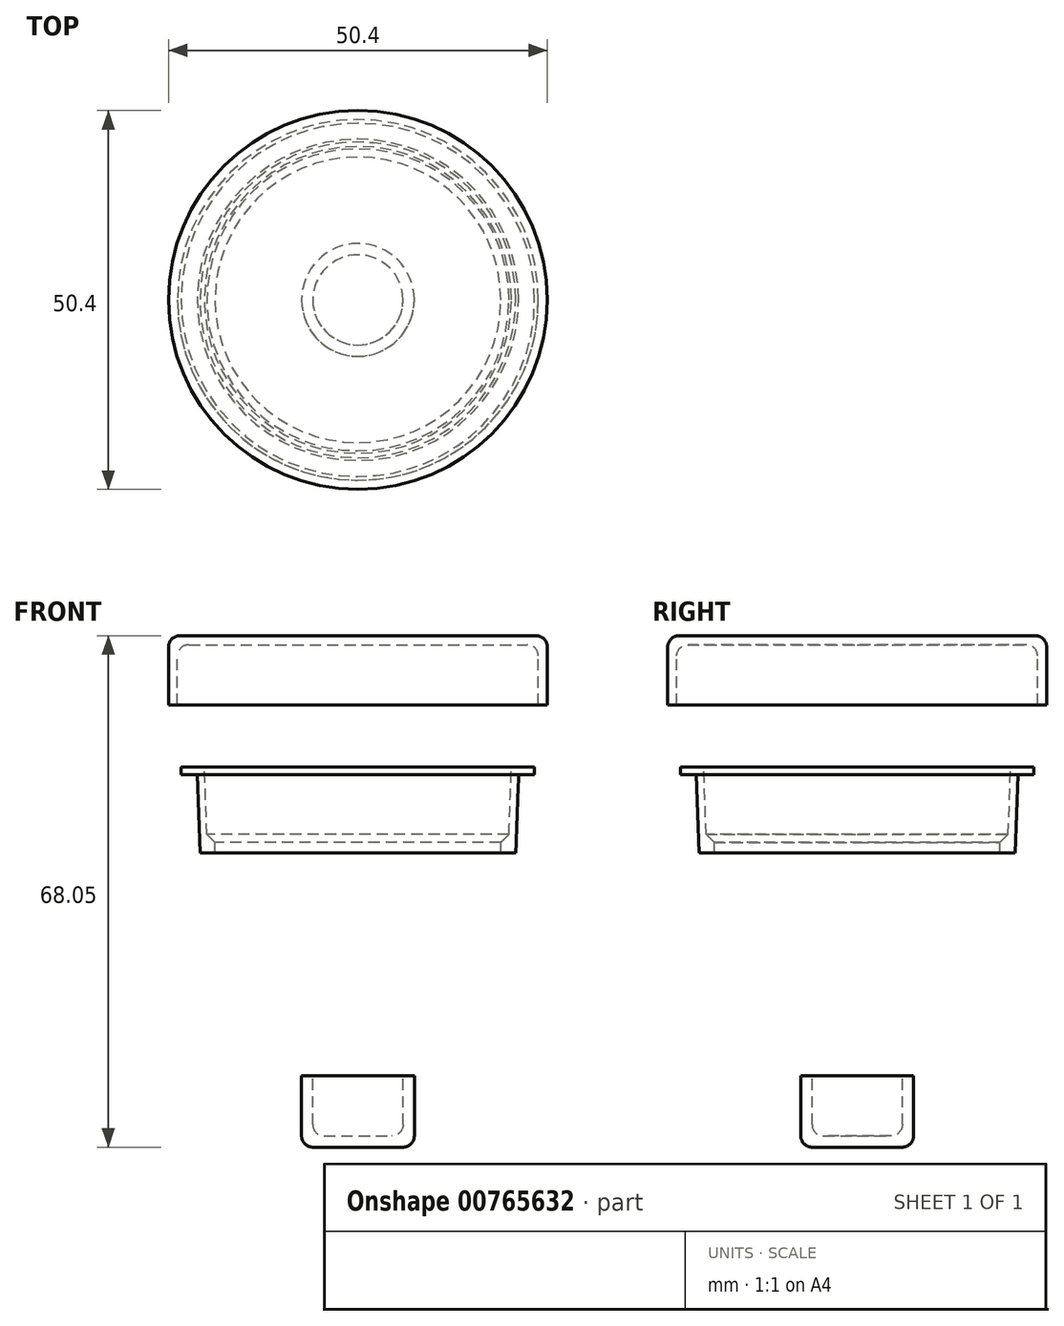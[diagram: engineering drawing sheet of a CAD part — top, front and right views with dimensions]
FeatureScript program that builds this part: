
annotation { "Feature Type Name" : "Feature", "Feature Type Description" : "" }
export const myFeature = defineFeature(function(context is Context, id is Id, definition is map)
    precondition{}
    {
        {
            var Q0;
            Q0=qCreatedBy(makeId("Front.planeOp"),FACE);
            var sketch = newSketch(context, id + "F0", { "sketchPlane" : qUnion([Q0])});
            skLineSegment(sketch, "E0", {"start": v(0, 66.35) * mm, "end": v(0, -60.94) * mm, "construction": true});
            skLineSegment(sketch, "E1", {"start": v(-23.5, 22.12) * mm, "end": v(-21.37, 22.12) * mm});
            skLineSegment(sketch, "E2", {"start": v(-21.38, 22.12) * mm, "end": v(-21, 11.72) * mm});
            skLineSegment(sketch, "E3", {"start": v(-21, 11.72) * mm, "end": v(-19, 11.72) * mm});
            skLineSegment(sketch, "E4.0", {"start": v(-23.5, 23.12) * mm, "end": v(-21.37, 23.12) * mm});
            skLineSegment(sketch, "E5.0", {"start": v(-20.38, 22.15) * mm, "end": v(-20.04, 12.72) * mm});
            skLineSegment(sketch, "E6", {"start": v(-20.04, 12.72) * mm, "end": v(-19, 12.72) * mm});
            skLineSegment(sketch, "E7", {"start": v(-20.38, 22.15) * mm, "end": v(-20.41, 23.12) * mm});
            skLineSegment(sketch, "E8", {"start": v(-21.37, 23.12) * mm, "end": v(-20.41, 23.12) * mm});
            skLineSegment(sketch, "E9", {"start": v(-23.5, 23.12) * mm, "end": v(-23.5, 22.12) * mm});
            skLineSegment(sketch, "E10", {"start": v(-19, 12.72) * mm, "end": v(-19, 11.72) * mm});
            skSolve(sketch);
        }
        {
            var Q0;
            Q0 = qSketchRegion(id + "F0", true);
            var Q1;
            Q1=sQuery(id+"F0.wireOp",EDGE,"E0");
            revolve(context, id + "F1", {"surfaceOperationType" : NewSurfaceOperationType.NEW, "entities" : qUnion([Q0]), "axis" : qUnion([Q1]), "revolveType" : RevolveType.FULL});
        }
        {
            var Q0;
            Q0=makeQuery(id+"F1.opRevolve","SWEPT_EDGE",EDGE,{"disambiguationData":[OSD([sQuery(id+"F0.wireOp",EDGE,"E5.0"),sQuery(id+"F0.wireOp",EDGE,"E6")])]});
            chamfer(context, id + "F2", {"entities" : qUnion([Q0]), "width" : 1.5 * mm, "tangentPropagation" : true});
        }
        {
            var Q0;
            Q0=qCreatedBy(makeId("Front.planeOp"),FACE);
            var sketch = newSketch(context, id + "F3", { "sketchPlane" : qUnion([Q0])});
            skLineSegment(sketch, "E11", {"start": v(-6, -17.94) * mm, "end": v(-6, -25.94) * mm});
            skLineSegment(sketch, "E12", {"start": v(-6, -25.94) * mm, "end": v(0, -25.94) * mm});
            skLineSegment(sketch, "E13", {"start": v(-6, -17.94) * mm, "end": v(-7.5, -17.94) * mm});
            skLineSegment(sketch, "E14", {"start": v(-7.5, -17.94) * mm, "end": v(-7.5, -27.44) * mm});
            skLineSegment(sketch, "E15", {"start": v(-7.5, -27.44) * mm, "end": v(0, -27.44) * mm});
            skLineSegment(sketch, "E16", {"start": v(0, -27.44) * mm, "end": v(0, -25.94) * mm});
            skSolve(sketch);
        }
        {
            var Q0;
            Q0=makeQuery(id+"F3.imprint","IMPRINT",FACE,{"disambiguationData":[TD([[makeQuery(id+"F3.imprint","IMPRINT",EDGE,{"derivedFrom":sQuery(id+"F3.wireOp",EDGE,"E11")}),-1.0]])]});
            var Q1;
            Q1=sQuery(id+"F0.wireOp",EDGE,"E0");
            revolve(context, id + "F4", {"surfaceOperationType" : NewSurfaceOperationType.NEW, "entities" : qUnion([Q0]), "axis" : qUnion([Q1]), "revolveType" : RevolveType.FULL});
        }
        {
            var Q0;
            Q0=qCreatedBy(makeId("Front.planeOp"),FACE);
            var sketch = newSketch(context, id + "F5", { "sketchPlane" : qUnion([Q0])});
            skLineSegment(sketch, "E17", {"start": v(-24, 31.41) * mm, "end": v(-24, 39.41) * mm});
            skLineSegment(sketch, "E18", {"start": v(-24, 39.41) * mm, "end": v(0, 39.41) * mm});
            skLineSegment(sketch, "E19", {"start": v(0, 39.41) * mm, "end": v(0, 40.61) * mm});
            skLineSegment(sketch, "E20", {"start": v(0, 40.61) * mm, "end": v(-25.2, 40.61) * mm});
            skLineSegment(sketch, "E21", {"start": v(-25.2, 40.61) * mm, "end": v(-25.2, 31.41) * mm});
            skLineSegment(sketch, "E22", {"start": v(-25.2, 31.41) * mm, "end": v(-24, 31.41) * mm});
            skSolve(sketch);
        }
        {
            var Q0;
            Q0 = qSketchRegion(id + "F5", true);
            var Q1;
            Q1=sQuery(id+"F0.wireOp",EDGE,"E0");
            revolve(context, id + "F6", {"surfaceOperationType" : NewSurfaceOperationType.NEW, "entities" : qUnion([Q0]), "axis" : qUnion([Q1]), "revolveType" : RevolveType.FULL});
        }
        {
            var Q0;
            Q0=makeQuery(id+"F6.opRevolve","SWEPT_EDGE",EDGE,{"disambiguationData":[OSD([sQuery(id+"F5.wireOp",EDGE,"E20"),sQuery(id+"F5.wireOp",EDGE,"E21")])]});
            var Q1;
            Q1=makeQuery(id+"F6.opRevolve","SWEPT_EDGE",EDGE,{"disambiguationData":[OSD([sQuery(id+"F5.wireOp",EDGE,"E17"),sQuery(id+"F5.wireOp",EDGE,"E18")])]});
            fillet(context, id + "F7", {"entities" : qUnion([Q0, Q1]), "radius" : 1.5 * mm, "tangentPropagation" : true, "allowEdgeOverflow" : false});
        }
        {
            var Q0;
            Q0=makeQuery(id+"F4.opRevolve","SWEPT_EDGE",EDGE,{"disambiguationData":[OSD([sQuery(id+"F3.wireOp",EDGE,"E14"),sQuery(id+"F3.wireOp",EDGE,"E15")])]});
            var Q1;
            Q1=makeQuery(id+"F4.opRevolve","SWEPT_FACE",FACE,{"disambiguationData":[OSD([sQuery(id+"F3.wireOp",EDGE,"E12")])]});
            fillet(context, id + "F8", {"entities" : qUnion([Q0, Q1]), "radius" : 1.5 * mm, "tangentPropagation" : true, "allowEdgeOverflow" : false});
        }
    });
